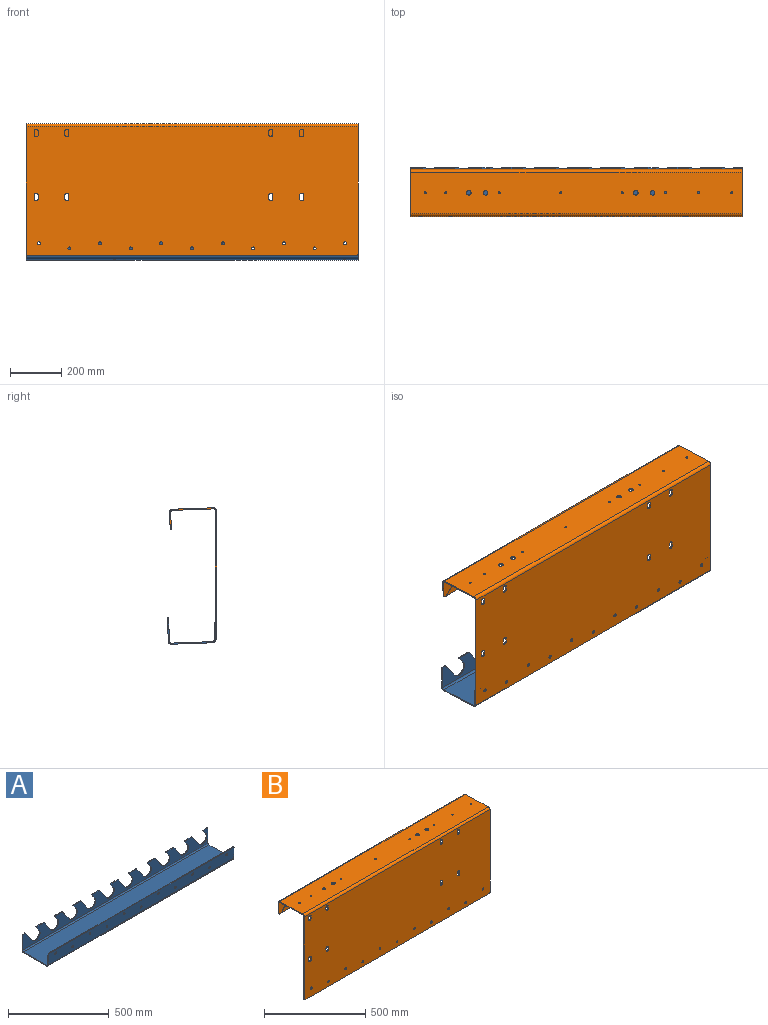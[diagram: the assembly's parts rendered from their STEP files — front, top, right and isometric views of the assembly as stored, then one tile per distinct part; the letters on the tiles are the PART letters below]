
ASSEMBLY  parts=2 mates=1
PART A: 99 faces, bbox 1300x187.1x104.5 mm
  f0: cylinder r=31mm len=56.39mm, axis (0,-1,0), area 438.3mm2, adj f1,f42,f43,f44
  f1: plane 26.82x18.78mm, normal (-0.82,0,-0.57), area 147.4mm2, adj f0,f43,f44,f64
  f2: plane 25.47x4.5mm, normal (0,0,1), area 114.6mm2, adj f43,f44,f52,f64
  f3: plane 87.9x4.5mm, normal (1,0,0), area 395.6mm2, adj f43,f44,f52,f95
  f4: plane 87.9x4.5mm, normal (-1,0,0), area 395.6mm2, adj f43,f44,f56,f96
  f5: plane 12.4x4.5mm, normal (0,0,1), area 55.8mm2, adj f43,f44,f56,f57
  f6: plane 63.4x44.39mm, normal (0.82,0,0.57), area 348.3mm2, adj f7,f43,f44,f57
  f7: cylinder r=31mm len=56.39mm, axis (0,-1,0), area 438.3mm2, adj f6,f8,f43,f44
  f8: plane 26.82x18.78mm, normal (-0.82,0,-0.57), area 147.4mm2, adj f7,f43,f44,f54
  f9: plane 47.87x4.5mm, normal (0,0,1), area 215.4mm2, adj f43,f44,f54,f60
  f10: plane 63.4x44.39mm, normal (0.82,0,0.57), area 348.3mm2, adj f11,f43,f44,f60
  f11: cylinder r=31mm len=56.39mm, axis (0,-1,0), area 438.3mm2, adj f10,f12,f43,f44
  f12: plane 26.82x18.78mm, normal (-0.82,0,-0.57), area 147.4mm2, adj f11,f43,f44,f59
  f13: plane 47.87x4.5mm, normal (0,0,1), area 215.4mm2, adj f43,f44,f51,f59
  f14: plane 63.4x44.39mm, normal (0.82,0,0.57), area 348.3mm2, adj f15,f43,f44,f51
  f15: cylinder r=31mm len=56.39mm, axis (0,-1,0), area 438.3mm2, adj f14,f16,f43,f44
  f16: plane 26.82x18.78mm, normal (-0.82,0,-0.57), area 147.4mm2, adj f15,f43,f44,f50
  f17: plane 47.87x4.5mm, normal (0,0,1), area 215.4mm2, adj f43,f44,f49,f50
  f18: plane 63.4x44.39mm, normal (0.82,0,0.57), area 348.3mm2, adj f19,f43,f44,f49
  f19: cylinder r=31mm len=56.39mm, axis (0,-1,0), area 438.3mm2, adj f18,f20,f43,f44
  f20: plane 26.82x18.78mm, normal (-0.82,0,-0.57), area 147.4mm2, adj f19,f43,f44,f48
  f21: plane 47.87x4.5mm, normal (0,0,1), area 215.4mm2, adj f43,f44,f48,f55
  f22: plane 63.4x44.39mm, normal (0.82,0,0.57), area 348.3mm2, adj f23,f43,f44,f55
  f23: cylinder r=31mm len=56.39mm, axis (0,-1,0), area 438.3mm2, adj f22,f24,f43,f44
  f24: plane 26.82x18.78mm, normal (-0.82,0,-0.57), area 147.4mm2, adj f23,f43,f44,f47
  f25: plane 47.87x4.5mm, normal (0,0,1), area 215.4mm2, adj f43,f44,f47,f53
  f26: plane 63.4x44.39mm, normal (0.82,0,0.57), area 348.3mm2, adj f27,f43,f44,f53
  f27: cylinder r=31mm len=56.39mm, axis (0,-1,0), area 438.3mm2, adj f26,f28,f43,f44
  f28: plane 26.82x18.78mm, normal (-0.82,0,-0.57), area 147.4mm2, adj f27,f43,f44,f46
  f29: plane 47.87x4.5mm, normal (0,0,1), area 215.4mm2, adj f43,f44,f46,f58
  f30: plane 63.4x44.39mm, normal (0.82,0,0.57), area 348.3mm2, adj f31,f43,f44,f58
  f31: cylinder r=31mm len=56.39mm, axis (0,-1,0), area 438.3mm2, adj f30,f32,f43,f44
  f32: plane 26.82x18.78mm, normal (-0.82,0,-0.57), area 147.4mm2, adj f31,f43,f44,f45
  f33: plane 47.87x4.5mm, normal (0,0,1), area 215.4mm2, adj f43,f44,f45,f61
  f34: plane 63.4x44.39mm, normal (0.82,0,0.57), area 348.3mm2, adj f35,f43,f44,f61
  f35: cylinder r=31mm len=56.39mm, axis (0,-1,0), area 438.3mm2, adj f34,f36,f43,f44
  f36: plane 26.82x18.78mm, normal (-0.82,0,-0.57), area 147.4mm2, adj f35,f43,f44,f62
  f37: plane 47.87x4.5mm, normal (0,0,1), area 215.4mm2, adj f43,f44,f62,f63
  f38: plane 63.4x44.39mm, normal (0.82,0,0.57), area 348.3mm2, adj f39,f43,f44,f63
  f39: cylinder r=31mm len=56.39mm, axis (0,-1,0), area 438.3mm2, adj f38,f40,f43,f44
  f40: plane 26.82x18.78mm, normal (-0.82,0,-0.57), area 147.4mm2, adj f39,f43,f44,f65
  f41: plane 47.87x4.5mm, normal (0,0,1), area 215.4mm2, adj f43,f44,f65,f66
  f42: plane 63.4x44.39mm, normal (0.82,0,0.57), area 348.3mm2, adj f0,f43,f44,f66
  f43: plane 1300x92.9mm, normal (0,1,0), area 69478.5mm2, adj f0,f1,f2,f3,f4,f5,f6,f7
  f44: plane 1300x92.9mm, normal (0,-1,0), area 69478.5mm2, adj f0,f1,f2,f3,f4,f5,f6,f7
  f45: cylinder r=2mm len=4.5mm, axis (0,1,0), area 19.6mm2, adj f32,f33,f43,f44
  f46: cylinder r=2mm len=4.5mm, axis (0,1,0), area 19.6mm2, adj f28,f29,f43,f44
  f47: cylinder r=2mm len=4.5mm, axis (0,1,0), area 19.6mm2, adj f24,f25,f43,f44
  f48: cylinder r=2mm len=4.5mm, axis (0,1,0), area 19.6mm2, adj f20,f21,f43,f44
  f49: cylinder r=5mm len=4.5mm, axis (0,1,0), area 21.6mm2, adj f17,f18,f43,f44
  f50: cylinder r=2mm len=4.5mm, axis (0,1,0), area 19.6mm2, adj f16,f17,f43,f44
  f51: cylinder r=5mm len=4.5mm, axis (0,1,0), area 21.6mm2, adj f13,f14,f43,f44
  f52: cylinder r=5mm len=5mm, axis (0,-1,0), area 35.3mm2, adj f2,f3,f43,f44
  f53: cylinder r=5mm len=4.5mm, axis (0,1,0), area 21.6mm2, adj f25,f26,f43,f44
  f54: cylinder r=2mm len=4.5mm, axis (0,1,0), area 19.6mm2, adj f8,f9,f43,f44
  f55: cylinder r=5mm len=4.5mm, axis (0,1,0), area 21.6mm2, adj f21,f22,f43,f44
  f56: cylinder r=5mm len=5mm, axis (0,1,0), area 35.3mm2, adj f4,f5,f43,f44
  f57: cylinder r=5mm len=4.5mm, axis (0,1,0), area 21.6mm2, adj f5,f6,f43,f44
  f58: cylinder r=5mm len=4.5mm, axis (0,1,0), area 21.6mm2, adj f29,f30,f43,f44
  f59: cylinder r=2mm len=4.5mm, axis (0,1,0), area 19.6mm2, adj f12,f13,f43,f44
  f60: cylinder r=5mm len=4.5mm, axis (0,1,0), area 21.6mm2, adj f9,f10,f43,f44
  f61: cylinder r=5mm len=4.5mm, axis (0,1,0), area 21.6mm2, adj f33,f34,f43,f44
  f62: cylinder r=2mm len=4.5mm, axis (0,1,0), area 19.6mm2, adj f36,f37,f43,f44
  f63: cylinder r=5mm len=4.5mm, axis (0,1,0), area 21.6mm2, adj f37,f38,f43,f44
  f64: cylinder r=2mm len=4.5mm, axis (0,1,0), area 19.6mm2, adj f1,f2,f43,f44
  f65: cylinder r=2mm len=4.5mm, axis (0,1,0), area 19.6mm2, adj f40,f41,f43,f44
  f66: cylinder r=5mm len=4.5mm, axis (0,1,0), area 21.6mm2, adj f41,f42,f43,f44
  f67: plane 161.54x4.5mm, normal (-1,0,0), area 726.9mm2, adj f71,f72,f92,f96
  f68: cylinder r=4mm len=8mm, axis (0,0,-1), area 113.1mm2, adj f71,f72
  f69: cylinder r=4mm len=8mm, axis (0,0,-1), area 113.1mm2, adj f71,f72
  f70: plane 161.54x4.5mm, normal (1,0,0), area 726.9mm2, adj f71,f72,f91,f95
  f71: plane 1300x161.54mm, normal (0,0,-1), area 209906.2mm2, adj f67,f68,f69,f70,f93,f97
  f72: plane 1300x161.54mm, normal (0,0,1), area 209906.2mm2, adj f67,f68,f69,f70,f94,f98
  f73: plane 1290x4.5mm, normal (0,-0.03,1), area 5805mm2, adj f87,f88,f89,f90
  f74: plane 63.92x6.72mm, normal (-1,0,0), area 287.1mm2, adj f87,f88,f89,f92
  f75: cylinder r=6mm len=12.15mm, axis (0,-1,-0.03), area 169.6mm2, adj f87,f88
  f76: cylinder r=6mm len=12.15mm, axis (0,-1,-0.03), area 169.6mm2, adj f87,f88
  f77: cylinder r=6mm len=12.15mm, axis (0,-1,-0.03), area 169.6mm2, adj f87,f88
  f78: cylinder r=6mm len=12.15mm, axis (0,-1,-0.03), area 169.6mm2, adj f87,f88
  f79: cylinder r=6mm len=12.15mm, axis (0,-1,-0.03), area 169.6mm2, adj f87,f88
  f80: cylinder r=6mm len=12.15mm, axis (0,-1,-0.03), area 169.6mm2, adj f87,f88
  f81: cylinder r=6mm len=12.15mm, axis (0,-1,-0.03), area 169.6mm2, adj f87,f88
  f82: cylinder r=6mm len=12.15mm, axis (0,-1,-0.03), area 169.6mm2, adj f87,f88
  f83: cylinder r=6mm len=12.15mm, axis (0,-1,-0.03), area 169.6mm2, adj f87,f88
  f84: cylinder r=6mm len=12.15mm, axis (0,-1,-0.03), area 169.6mm2, adj f87,f88
  f85: cylinder r=6mm len=12.15mm, axis (0,-1,-0.03), area 169.6mm2, adj f87,f88
  f86: plane 63.92x6.72mm, normal (1,0,0), area 287.1mm2, adj f87,f88,f90,f91
  f87: plane 1300x68.76mm, normal (0,-1,-0.03), area 88182.6mm2, adj f73,f74,f75,f76,f77,f78,f79,f80
  f88: plane 1300x68.76mm, normal (0,1,0.03), area 88182.6mm2, adj f73,f74,f75,f76,f77,f78,f79,f80
  f89: cylinder r=5mm len=5.15mm, axis (0,-1,-0.03), area 35.3mm2, adj f73,f74,f87,f88
  f90: cylinder r=5mm len=5.15mm, axis (0,-1,-0.03), area 35.3mm2, adj f73,f86,f87,f88
  f91: plane 11.59x11.35mm, normal (1,0,0), area 64.6mm2, adj f70,f86,f93,f94
  f92: plane 11.59x11.35mm, normal (-1,0,0), area 64.6mm2, adj f67,f74,f93,f94
  f93: cylinder r=11.6mm len=1300mm, axis (1,0,0), area 23161.2mm2, adj f71,f87,f91,f92
  f94: cylinder r=7.1mm len=1300mm, axis (1,0,0), area 14176.3mm2, adj f72,f88,f91,f92
  f95: plane 11.6x11.6mm, normal (1,0,0), area 66.1mm2, adj f3,f70,f97,f98
  f96: plane 11.6x11.6mm, normal (-1,0,0), area 66.1mm2, adj f4,f67,f97,f98
  f97: cylinder r=11.6mm len=1300mm, axis (1,0,0), area 23687.6mm2, adj f43,f71,f95,f96
  f98: cylinder r=7.1mm len=1300mm, axis (1,0,0), area 14498.5mm2, adj f44,f72,f95,f96
PART B: 141 faces, bbox 1300x184x516.2 mm
  f0: plane 14x4.5mm, normal (-1,0,0), area 63mm2, adj f30,f31,f44,f49
  f1: plane 14x4.5mm, normal (1,0,0), area 63mm2, adj f30,f31,f44,f49
  f2: plane 14x4.5mm, normal (-1,0,0), area 63mm2, adj f30,f31,f43,f45
  f3: plane 14x4.5mm, normal (-1,0,0), area 63mm2, adj f30,f31,f46,f47
  f4: plane 14x4.5mm, normal (-1,0,0), area 63mm2, adj f30,f31,f41,f48
  f5: plane 499.65x4.5mm, normal (1,0,0), area 2248.4mm2, adj f30,f31,f42,f138
  f6: plane 1290x4.5mm, normal (0,0,-1), area 5805mm2, adj f30,f31,f40,f42
  f7: plane 499.65x4.5mm, normal (-1,0,0), area 2248.4mm2, adj f30,f31,f40,f137
  f8: plane 14x4.5mm, normal (-1,0,0), area 63mm2, adj f30,f31,f38,f39
  f9: plane 14x4.5mm, normal (-1,0,0), area 63mm2, adj f30,f31,f36,f37
  f10: plane 14x4.5mm, normal (-1,0,0), area 63mm2, adj f30,f31,f33,f35
  f11: plane 14x4.5mm, normal (-1,0,0), area 63mm2, adj f30,f31,f32,f34
  f12: plane 14x4.5mm, normal (1,0,0), area 63mm2, adj f30,f31,f32,f34
  f13: cylinder r=6mm len=12mm, axis (0,-1,0), area 169.6mm2, adj f30,f31
  f14: cylinder r=6mm len=12mm, axis (0,-1,0), area 169.6mm2, adj f30,f31
  f15: cylinder r=6mm len=12mm, axis (0,-1,0), area 169.6mm2, adj f30,f31
  f16: cylinder r=6mm len=12mm, axis (0,-1,0), area 169.6mm2, adj f30,f31
  f17: cylinder r=6mm len=12mm, axis (0,-1,0), area 169.6mm2, adj f30,f31
  f18: cylinder r=6mm len=12mm, axis (0,-1,0), area 169.6mm2, adj f30,f31
  f19: cylinder r=6mm len=12mm, axis (0,-1,0), area 169.6mm2, adj f30,f31
  f20: cylinder r=6mm len=12mm, axis (0,-1,0), area 169.6mm2, adj f30,f31
  f21: cylinder r=6mm len=12mm, axis (0,-1,0), area 169.6mm2, adj f30,f31
  f22: cylinder r=6mm len=12mm, axis (0,-1,0), area 169.6mm2, adj f30,f31
  f23: cylinder r=6mm len=12mm, axis (0,-1,0), area 169.6mm2, adj f30,f31
  f24: plane 14x4.5mm, normal (1,0,0), area 63mm2, adj f30,f31,f33,f35
  f25: plane 14x4.5mm, normal (1,0,0), area 63mm2, adj f30,f31,f36,f37
  f26: plane 14x4.5mm, normal (1,0,0), area 63mm2, adj f30,f31,f38,f39
  f27: plane 14x4.5mm, normal (1,0,0), area 63mm2, adj f30,f31,f41,f48
  f28: plane 14x4.5mm, normal (1,0,0), area 63mm2, adj f30,f31,f46,f47
  f29: plane 14x4.5mm, normal (1,0,0), area 63mm2, adj f30,f31,f43,f45
  f30: plane 1300x504.65mm, normal (0,1,0), area 651386.8mm2, adj f0,f1,f2,f3,f4,f5,f6,f7
  f31: plane 1300x504.65mm, normal (0,-1,0), area 651386.8mm2, adj f0,f1,f2,f3,f4,f5,f6,f7
  f32: cylinder r=8mm len=16mm, axis (0,1,0), area 113.1mm2, adj f11,f12,f30,f31
  f33: cylinder r=8mm len=16mm, axis (0,-1,0), area 113.1mm2, adj f10,f24,f30,f31
  f34: cylinder r=8mm len=16mm, axis (0,1,0), area 113.1mm2, adj f11,f12,f30,f31
  f35: cylinder r=8mm len=16mm, axis (0,-1,0), area 113.1mm2, adj f10,f24,f30,f31
  f36: cylinder r=8mm len=16mm, axis (0,-1,0), area 113.1mm2, adj f9,f25,f30,f31
  f37: cylinder r=8mm len=16mm, axis (0,-1,0), area 113.1mm2, adj f9,f25,f30,f31
  f38: cylinder r=8mm len=16mm, axis (0,-1,0), area 113.1mm2, adj f8,f26,f30,f31
  f39: cylinder r=8mm len=16mm, axis (0,-1,0), area 113.1mm2, adj f8,f26,f30,f31
  f40: cylinder r=5mm len=5mm, axis (0,-1,0), area 35.3mm2, adj f6,f7,f30,f31
  f41: cylinder r=8mm len=16mm, axis (0,-1,0), area 113.1mm2, adj f4,f27,f30,f31
  f42: cylinder r=5mm len=5mm, axis (0,1,0), area 35.3mm2, adj f5,f6,f30,f31
  f43: cylinder r=8mm len=16mm, axis (0,1,0), area 113.1mm2, adj f2,f29,f30,f31
  f44: cylinder r=8mm len=16mm, axis (0,-1,0), area 113.1mm2, adj f0,f1,f30,f31
  f45: cylinder r=8mm len=16mm, axis (0,1,0), area 113.1mm2, adj f2,f29,f30,f31
  f46: cylinder r=8mm len=16mm, axis (0,1,0), area 113.1mm2, adj f3,f28,f30,f31
  f47: cylinder r=8mm len=16mm, axis (0,1,0), area 113.1mm2, adj f3,f28,f30,f31
  f48: cylinder r=8mm len=16mm, axis (0,1,0), area 113.1mm2, adj f4,f27,f30,f31
  f49: cylinder r=8mm len=16mm, axis (0,1,0), area 113.1mm2, adj f0,f1,f30,f31
  f50: plane 160.95x10.11mm, normal (1,0,0), area 724mm2, adj f64,f65,f133,f138
  f51: cylinder r=9mm len=18.15mm, axis (0,-0.03,-1), area 254.5mm2, adj f64,f65
  f52: cylinder r=9mm len=18.15mm, axis (0,-0.03,-1), area 254.5mm2, adj f64,f65
  f53: cylinder r=9mm len=18.15mm, axis (0,-0.03,-1), area 254.5mm2, adj f64,f65
  f54: cylinder r=9mm len=18.15mm, axis (0,-0.03,-1), area 254.5mm2, adj f64,f65
  f55: cylinder r=4mm len=8.15mm, axis (0,-0.03,-1), area 113.1mm2, adj f64,f65
  f56: cylinder r=4mm len=8.15mm, axis (0,-0.03,-1), area 113.1mm2, adj f64,f65
  f57: cylinder r=4mm len=8.15mm, axis (0,-0.03,-1), area 113.1mm2, adj f64,f65
  f58: cylinder r=4mm len=8.15mm, axis (0,-0.03,-1), area 113.1mm2, adj f64,f65
  f59: cylinder r=4mm len=8.15mm, axis (0,-0.03,-1), area 113.1mm2, adj f64,f65
  f60: cylinder r=4mm len=8.15mm, axis (0,-0.03,-1), area 113.1mm2, adj f64,f65
  f61: cylinder r=4mm len=8.15mm, axis (0,-0.03,-1), area 113.1mm2, adj f64,f65
  f62: cylinder r=4mm len=8.15mm, axis (0,-0.03,-1), area 113.1mm2, adj f64,f65
  f63: plane 160.95x10.11mm, normal (-1,0,0), area 724mm2, adj f64,f65,f134,f137
  f64: plane 1300x160.79mm, normal (0,-0.03,-1), area 207734.2mm2, adj f50,f51,f52,f53,f54,f55,f56,f57
  f65: plane 1300x160.79mm, normal (0,0.03,1), area 207734.2mm2, adj f50,f51,f52,f53,f54,f55,f56,f57
  f66: plane 63.52x6.71mm, normal (-1,0,0), area 285.3mm2, adj f99,f100,f120,f134
  f67: plane 4.93x4.5mm, normal (0,-0.03,-1), area 22.2mm2, adj f99,f100,f118,f120
  f68: plane 63x62.88mm, normal (0.71,-0.02,-0.71), area 400.2mm2, adj f99,f100,f118,f119
  f69: plane 59.64x59.52mm, normal (-0.71,0.02,0.71), area 378.8mm2, adj f99,f100,f116,f119
  f70: plane 120.27x4.5mm, normal (0,-0.03,-1), area 541.2mm2, adj f99,f100,f116,f122
  f71: plane 63x62.88mm, normal (0.71,-0.02,-0.71), area 400.2mm2, adj f99,f100,f122,f123
  f72: plane 59.64x59.52mm, normal (-0.71,0.02,0.71), area 378.8mm2, adj f99,f100,f121,f123
  f73: plane 120.27x4.5mm, normal (0,-0.03,-1), area 541.2mm2, adj f99,f100,f121,f125
  f74: plane 63x62.88mm, normal (0.71,-0.02,-0.71), area 400.2mm2, adj f99,f100,f125,f126
  f75: plane 59.64x59.52mm, normal (-0.71,0.02,0.71), area 378.8mm2, adj f99,f100,f124,f126
  f76: plane 120.27x4.5mm, normal (0,-0.03,-1), area 541.2mm2, adj f99,f100,f114,f124
  f77: plane 63x62.88mm, normal (0.71,-0.02,-0.71), area 400.2mm2, adj f99,f100,f113,f114
  f78: plane 59.64x59.52mm, normal (-0.71,0.02,0.71), area 378.8mm2, adj f99,f100,f113,f115
  f79: plane 120.27x4.5mm, normal (0,-0.03,-1), area 541.2mm2, adj f99,f100,f111,f115
  f80: plane 63x62.88mm, normal (0.71,-0.02,-0.71), area 400.2mm2, adj f99,f100,f110,f111
  f81: plane 59.64x59.52mm, normal (-0.71,0.02,0.71), area 378.8mm2, adj f99,f100,f110,f112
  f82: plane 120.27x4.5mm, normal (0,-0.03,-1), area 541.2mm2, adj f99,f100,f108,f112
  f83: plane 63x62.88mm, normal (0.71,-0.02,-0.71), area 400.2mm2, adj f99,f100,f107,f108
  f84: plane 59.64x59.52mm, normal (-0.71,0.02,0.71), area 378.8mm2, adj f99,f100,f107,f109
  f85: plane 120.27x4.5mm, normal (0,-0.03,-1), area 541.2mm2, adj f99,f100,f105,f109
  f86: plane 63x62.88mm, normal (0.71,-0.02,-0.71), area 400.2mm2, adj f99,f100,f104,f105
  f87: plane 59.64x59.52mm, normal (-0.71,0.02,0.71), area 378.8mm2, adj f99,f100,f104,f106
  f88: plane 120.27x4.5mm, normal (0,-0.03,-1), area 541.2mm2, adj f99,f100,f102,f106
  f89: plane 63x62.88mm, normal (0.71,-0.02,-0.71), area 400.2mm2, adj f99,f100,f101,f102
  f90: plane 59.64x59.52mm, normal (-0.71,0.02,0.71), area 378.8mm2, adj f99,f100,f101,f103
  f91: plane 120.27x4.5mm, normal (0,-0.03,-1), area 541.2mm2, adj f99,f100,f103,f128
  f92: plane 63x62.88mm, normal (0.71,-0.02,-0.71), area 400.2mm2, adj f99,f100,f128,f129
  f93: plane 59.64x59.52mm, normal (-0.71,0.02,0.71), area 378.8mm2, adj f99,f100,f127,f129
  f94: plane 120.27x4.5mm, normal (0,-0.03,-1), area 541.2mm2, adj f99,f100,f127,f131
  f95: plane 63x62.88mm, normal (0.71,-0.02,-0.71), area 400.2mm2, adj f99,f100,f131,f132
  f96: plane 59.64x59.52mm, normal (-0.71,0.02,0.71), area 378.8mm2, adj f99,f100,f130,f132
  f97: plane 105.34x4.5mm, normal (0,-0.03,-1), area 474mm2, adj f99,f100,f117,f130
  f98: plane 63.52x6.71mm, normal (1,0,0), area 285.3mm2, adj f99,f100,f117,f133
  f99: plane 1300x68.36mm, normal (0,-1,0.03), area 87038.7mm2, adj f66,f67,f68,f69,f70,f71,f72,f73
  f100: plane 1300x68.36mm, normal (0,1,-0.03), area 87038.7mm2, adj f66,f67,f68,f69,f70,f71,f72,f73
  f101: cylinder r=1mm len=4.56mm, axis (0,-1,0.03), area 14.1mm2, adj f89,f90,f99,f100
  f102: cylinder r=5mm len=4.55mm, axis (0,1,-0.03), area 17.7mm2, adj f88,f89,f99,f100
  f103: cylinder r=2mm len=4.62mm, axis (0,1,-0.03), area 21.2mm2, adj f90,f91,f99,f100
  f104: cylinder r=1mm len=4.56mm, axis (0,-1,0.03), area 14.1mm2, adj f86,f87,f99,f100
  f105: cylinder r=5mm len=4.55mm, axis (0,1,-0.03), area 17.7mm2, adj f85,f86,f99,f100
  f106: cylinder r=2mm len=4.62mm, axis (0,1,-0.03), area 21.2mm2, adj f87,f88,f99,f100
  f107: cylinder r=1mm len=4.56mm, axis (0,-1,0.03), area 14.1mm2, adj f83,f84,f99,f100
  f108: cylinder r=5mm len=4.55mm, axis (0,1,-0.03), area 17.7mm2, adj f82,f83,f99,f100
  f109: cylinder r=2mm len=4.62mm, axis (0,1,-0.03), area 21.2mm2, adj f84,f85,f99,f100
  f110: cylinder r=1mm len=4.56mm, axis (0,-1,0.03), area 14.1mm2, adj f80,f81,f99,f100
  f111: cylinder r=5mm len=4.55mm, axis (0,1,-0.03), area 17.7mm2, adj f79,f80,f99,f100
  f112: cylinder r=2mm len=4.62mm, axis (0,1,-0.03), area 21.2mm2, adj f81,f82,f99,f100
  f113: cylinder r=1mm len=4.56mm, axis (0,-1,0.03), area 14.1mm2, adj f77,f78,f99,f100
  f114: cylinder r=5mm len=4.55mm, axis (0,1,-0.03), area 17.7mm2, adj f76,f77,f99,f100
  f115: cylinder r=2mm len=4.62mm, axis (0,1,-0.03), area 21.2mm2, adj f78,f79,f99,f100
  f116: cylinder r=2mm len=4.62mm, axis (0,1,-0.03), area 21.2mm2, adj f69,f70,f99,f100
  f117: cylinder r=5mm len=5.15mm, axis (0,-1,0.03), area 35.3mm2, adj f97,f98,f99,f100
  f118: cylinder r=5mm len=4.55mm, axis (0,1,-0.03), area 17.7mm2, adj f67,f68,f99,f100
  f119: cylinder r=1mm len=4.56mm, axis (0,-1,0.03), area 14.1mm2, adj f68,f69,f99,f100
  f120: cylinder r=5mm len=5.15mm, axis (0,-1,0.03), area 35.3mm2, adj f66,f67,f99,f100
  f121: cylinder r=2mm len=4.62mm, axis (0,1,-0.03), area 21.2mm2, adj f72,f73,f99,f100
  f122: cylinder r=5mm len=4.55mm, axis (0,1,-0.03), area 17.7mm2, adj f70,f71,f99,f100
  f123: cylinder r=1mm len=4.56mm, axis (0,-1,0.03), area 14.1mm2, adj f71,f72,f99,f100
  f124: cylinder r=2mm len=4.62mm, axis (0,1,-0.03), area 21.2mm2, adj f75,f76,f99,f100
  f125: cylinder r=5mm len=4.55mm, axis (0,1,-0.03), area 17.7mm2, adj f73,f74,f99,f100
  f126: cylinder r=1mm len=4.56mm, axis (0,-1,0.03), area 14.1mm2, adj f74,f75,f99,f100
  f127: cylinder r=2mm len=4.62mm, axis (0,1,-0.03), area 21.2mm2, adj f93,f94,f99,f100
  f128: cylinder r=5mm len=4.55mm, axis (0,1,-0.03), area 17.7mm2, adj f91,f92,f99,f100
  f129: cylinder r=1mm len=4.56mm, axis (0,-1,0.03), area 14.1mm2, adj f92,f93,f99,f100
  f130: cylinder r=2mm len=4.62mm, axis (0,1,-0.03), area 21.2mm2, adj f96,f97,f99,f100
  f131: cylinder r=5mm len=4.55mm, axis (0,1,-0.03), area 17.7mm2, adj f94,f95,f99,f100
  f132: cylinder r=1mm len=4.56mm, axis (0,-1,0.03), area 14.1mm2, adj f95,f96,f99,f100
  f133: plane 12x11.35mm, normal (1,0,0), area 66.1mm2, adj f50,f98,f135,f136
  f134: plane 12x11.35mm, normal (-1,0,0), area 66.1mm2, adj f63,f66,f135,f136
  f135: cylinder r=11.6mm len=1300mm, axis (1,0,0), area 23687.6mm2, adj f65,f100,f133,f134
  f136: cylinder r=7.1mm len=1300mm, axis (1,0,0), area 14498.5mm2, adj f64,f99,f133,f134
  f137: plane 12.01x11.6mm, normal (-1,0,0), area 67.6mm2, adj f7,f63,f139,f140
  f138: plane 12.01x11.6mm, normal (1,0,0), area 67.6mm2, adj f5,f50,f139,f140
  f139: cylinder r=11.6mm len=1300mm, axis (-1,0,0), area 24214mm2, adj f31,f65,f137,f138
  f140: cylinder r=7.1mm len=1300mm, axis (-1,0,0), area 14820.6mm2, adj f30,f64,f137,f138
PLACE A rot(axis=(-1,0,0),2deg) t=(0,184.39,-13.94)mm
PLACE B at identity fixed
MATE fastened A.f75 <-> B.f13  axis (0,-1,0) through (1250,0,48)mm
